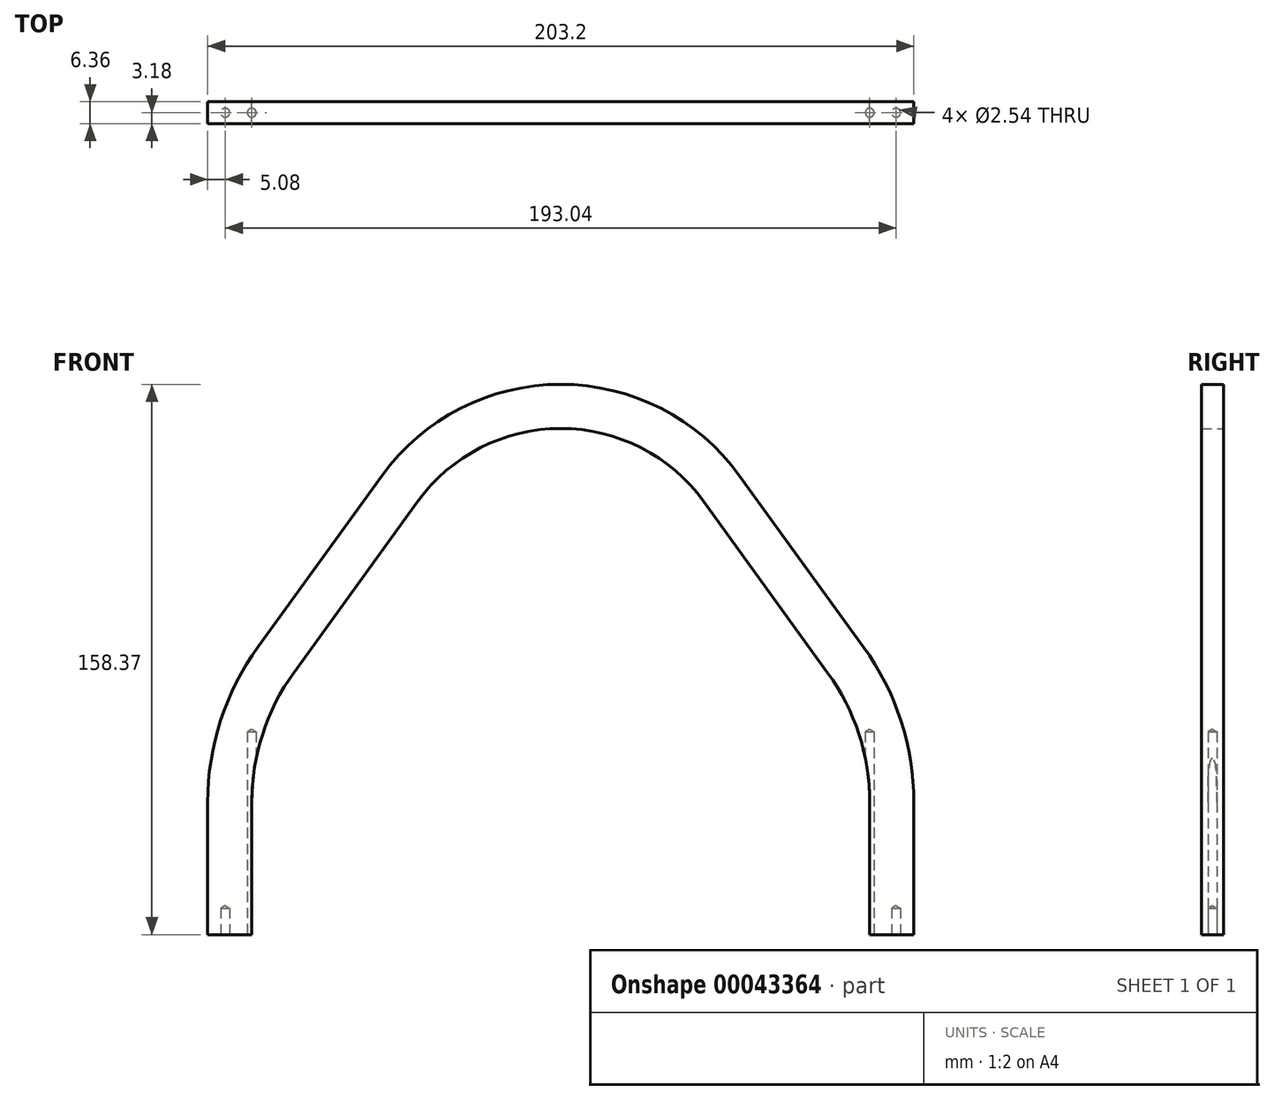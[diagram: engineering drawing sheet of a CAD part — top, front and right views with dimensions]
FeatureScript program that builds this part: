
annotation { "Feature Type Name" : "Feature", "Feature Type Description" : "" }
export const myFeature = defineFeature(function(context is Context, id is Id, definition is map)
    precondition{}
    {
        {
            var Q0;
            Q0=qCreatedBy(makeId("Front.planeOp"),FACE);
            var sketch = newSketch(context, id + "F0", { "sketchPlane" : qUnion([Q0])});
            skLineSegment(sketch, "E0", {"start": v(0, 0) * mm, "end": v(0, 203.2) * mm, "construction": true});
            skLineSegment(sketch, "E1", {"start": v(-101.6, 0) * mm, "end": v(101.6, 0) * mm, "construction": true});
            skLineSegment(sketch, "E2", {"start": v(-101.6, 0) * mm, "end": v(-101.6, 38.1) * mm});
            skLineSegment(sketch, "E3", {"start": v(-87.14, 82.77) * mm, "end": v(-51.45, 132.1) * mm});
            skPoint(sketch, "E4.visualSharp", {"position": v(-101.6, 62.78) * mm});
            skArc(sketch, "E4.filletArc", {"start": v(-87.14, 82.77) * mm, "mid": v(-97.9, 61.58) * mm, "end": v(-101.6, 38.1) * mm});
            skLineSegment(sketch, "E5.MirrorCS", {"start": v(101.6, 0) * mm, "end": v(101.6, 38.1) * mm});
            skArc(sketch, "E6.MirrorCS", {"start": v(87.14, 82.77) * mm, "mid": v(97.9, 61.58) * mm, "end": v(101.6, 38.1) * mm});
            skLineSegment(sketch, "E7.MirrorCS", {"start": v(87.14, 82.77) * mm, "end": v(51.45, 132.1) * mm});
            skPoint(sketch, "E8.visualSharp", {"position": v(0, 203.2) * mm});
            skArc(sketch, "E8.filletArc", {"start": v(51.45, 132.1) * mm, "mid": v(0, 158.37) * mm, "end": v(-51.45, 132.1) * mm});
            skLineSegment(sketch, "E9.0", {"start": v(76.85, 75.32) * mm, "end": v(41.16, 124.65) * mm});
            skLineSegment(sketch, "E9.1", {"start": v(-88.9, 0) * mm, "end": v(-88.9, 38.1) * mm});
            skArc(sketch, "E9.2", {"start": v(-76.85, 75.32) * mm, "mid": v(-85.81, 57.66) * mm, "end": v(-88.9, 38.1) * mm});
            skLineSegment(sketch, "E9.3", {"start": v(-76.85, 75.32) * mm, "end": v(-41.16, 124.65) * mm});
            skArc(sketch, "E9.4", {"start": v(41.16, 124.65) * mm, "mid": v(0, 145.67) * mm, "end": v(-41.16, 124.65) * mm});
            skLineSegment(sketch, "E10.0", {"start": v(88.9, 0) * mm, "end": v(88.9, 38.1) * mm});
            skArc(sketch, "E10.1", {"start": v(76.85, 75.32) * mm, "mid": v(85.81, 57.66) * mm, "end": v(88.9, 38.1) * mm});
            skLineSegment(sketch, "E11", {"start": v(-101.6, 0) * mm, "end": v(-88.9, 0) * mm});
            skLineSegment(sketch, "E12", {"start": v(88.9, 0) * mm, "end": v(101.6, 0) * mm});
            skSolve(sketch);
        }
        {
            var Q0;
            Q0 = qSketchRegion(id + "F0", true);
            extrude(context, id + "F1", {"entities" : qUnion([Q0]), "endBound" : BoundingType.SYMMETRIC, "depth" : 6.35 * mm});
        }
        {
            var Q0;
            Q0=qCreatedBy(makeId("Top.planeOp"),FACE);
            var sketch = newSketch(context, id + "F2", { "sketchPlane" : qUnion([Q0])});
            skLineSegment(sketch, "E13", {"start": v(-88.9, 0) * mm, "end": v(88.9, 0) * mm});
            skLineSegment(sketch, "E14", {"start": v(-88.9, 0) * mm, "end": v(-96.52, 0) * mm});
            skLineSegment(sketch, "E15", {"start": v(88.9, 0) * mm, "end": v(96.52, 0) * mm});
            skSolve(sketch);
        }
        {
            var Q0;
            Q0=sQuery(id+"F2.wireOp",VERTEX,"E14.end");
            var Q1;
            Q1=sQuery(id+"F2.wireOp",VERTEX,"E14.start");
            var Q2;
            Q2=sQuery(id+"F2.wireOp",VERTEX,"E13.end");
            var Q3;
            Q3=sQuery(id+"F2.wireOp",VERTEX,"E15.end");
            var Q4;
            Q4=makeQuery(id+"F1.opExtrude","SWEPT_BODY",BODY,{"disambiguationData":[OSD([sQuery(id+"F0.wireOp",EDGE,"E2"),sQuery(id+"F0.wireOp",EDGE,"E3"),sQuery(id+"F0.wireOp",EDGE,"E4.filletArc"),sQuery(id+"F0.wireOp",EDGE,"E5.MirrorCS"),sQuery(id+"F0.wireOp",EDGE,"E6.MirrorCS"),sQuery(id+"F0.wireOp",EDGE,"E7.MirrorCS"),sQuery(id+"F0.wireOp",EDGE,"E8.filletArc"),sQuery(id+"F0.wireOp",EDGE,"E9.0"),sQuery(id+"F0.wireOp",EDGE,"E9.1"),sQuery(id+"F0.wireOp",EDGE,"E9.2"),sQuery(id+"F0.wireOp",EDGE,"E9.3"),sQuery(id+"F0.wireOp",EDGE,"E9.4"),sQuery(id+"F0.wireOp",EDGE,"E10.0"),sQuery(id+"F0.wireOp",EDGE,"E10.1"),sQuery(id+"F0.wireOp",EDGE,"E11"),sQuery(id+"F0.wireOp",EDGE,"E12")])]});
            hole(context, id + "F3", {"style" : HoleStyle.SIMPLE, "holeDiameter" : 2.54 * mm, "endStyle" : HoleEndStyle.BLIND, "oppositeDirection" : true, "holeDepth" : 7.62 * mm, "locations" : qUnion([Q0, Q1, Q2, Q3]), "scope" : qUnion([Q4])});
        }
    });
